# Revit family: deceuninck_balkonniy_blok_leviy_dvustvorchatiy
name_source: partatom
category: Windows
revit_build: Autodesk Revit 2016 (Build: 20150506_1715(x64)
units: mm (PartAtom-declared; Revit-internal decimal feet)

## family parameters
Always vertical = Yes
Cut with Voids When Loaded = No
Host = Wall
OmniClass Number = 23.30.20.00
OmniClass Title = Windows
Room Calculation Point = No
Shared = No

## types (1)
- Энвин ЭКО-60
    Analytic Construction = <Нет>
    Height = 0 mm  [stored 0 ft]
    Rough Height = 0 mm  [stored 0 ft]
    Rough Width = 0 mm  [stored 0 ft]
    Rед = 1.0000 (m²·K)/W
    Rпрофиля = 0.6800 (m²·K)/W
    Rстеклопакета = 0.7600 (m²·K)/W
    Wall Closure = By host
    Width = 0 mm  [stored 0 ft]
    λ краевой зоны стеклопакета = 0.0600 (m²·K)/W
    Артикул импоста/армирование импоста = TE 60D  /  20 x 35
    Артикул рамы/армирование рамы = LE 60D  /  AR1
    Артикул створки/армирование рстворки = ZE 60D  /  AR1
    Высота порога = 80 mm
    Высота профиля имоста = 82 mm  [stored 0.269029 ft]
    Высота профиля рамы = 62 mm  [stored 0.203412 ft]
    Высота профиля створки = 76 mm  [stored 0.249344 ft]
    Высота расположения ручки = 1000 mm  [stored 3.28084 ft]
    ГОСТ = ГОСТ 30673-2013
    Класс профиля = Тип В
    Материал-Подоконник = ПВХ, белый
    Материал-Рама = <By Category>
    Материал-Стеклопакет = <By Category>
    Монтажный зазор.Боковой = 20 mm  [stored 0.0656168 ft]
    Наименование = Балконный блок левый двустворчатый Энвин ЭКО-60
    Огнестойкость = E-15
    Профильная система = Энвин ЭКО 60
    Стеклопакет.Толщина = 32 mm  [stored 0.104987 ft]
    Толщина стеклопакета = 32
    Ширина профиля = 60 mm  [stored 0.19685 ft]

note: [stored X ft] marks values corroborated as IEEE doubles in the binary element streams (Revit-internal decimal feet)

## geometry (parser evidence)
native form markers: Blend x2
no freeform markers — native parametric forms only
